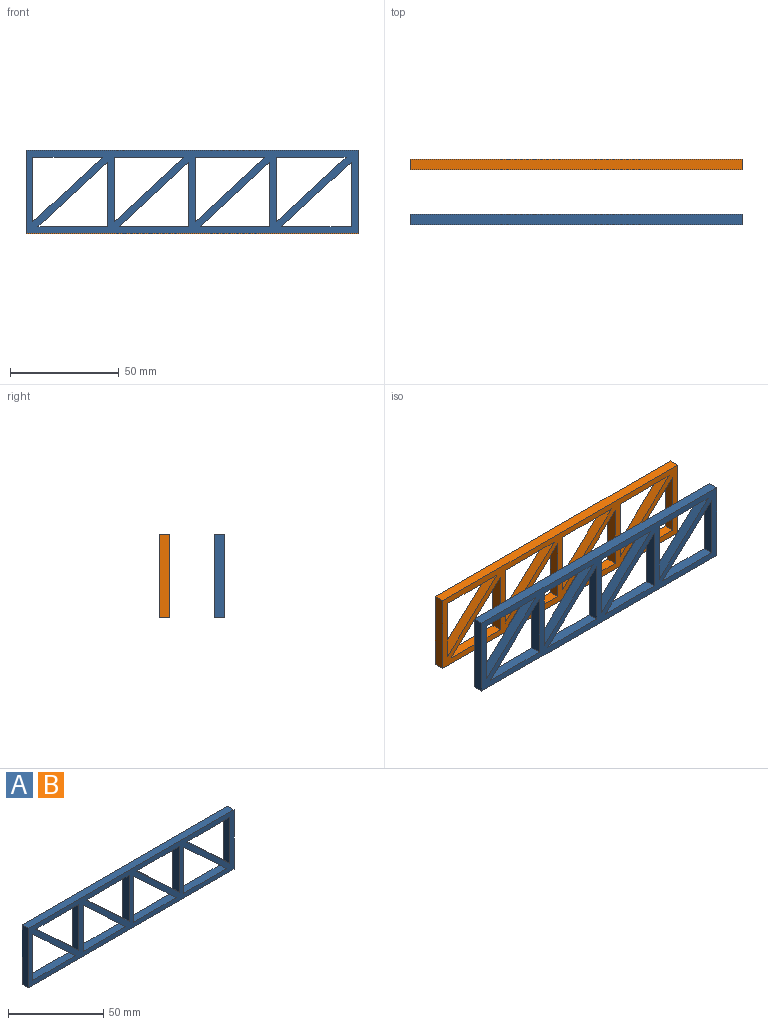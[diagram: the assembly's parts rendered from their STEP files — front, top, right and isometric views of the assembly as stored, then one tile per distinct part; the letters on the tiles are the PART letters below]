
ASSEMBLY  parts=2 mates=3
PART A: 30 faces, bbox 152.4x4.8x38.1 mm
  f0: plane 29.58x4.76mm, normal (1,0,0), area 140.9mm2, adj f1,f27,f28,f29
  f1: plane 31.8x29.58mm, normal (-0.68,0,-0.73), area 206.8mm2, adj f0,f27,f28,f29
  f2: plane 29.58x4.76mm, normal (1,0,0), area 140.9mm2, adj f3,f19,f28,f29
  f3: plane 31.8x29.58mm, normal (-0.68,0,-0.73), area 206.8mm2, adj f2,f19,f28,f29
  f4: plane 29.58x4.76mm, normal (1,0,0), area 140.9mm2, adj f5,f20,f28,f29
  f5: plane 31.8x29.58mm, normal (-0.68,0,-0.73), area 206.8mm2, adj f4,f20,f28,f29
  f6: plane 29.58x4.76mm, normal (1,0,0), area 140.9mm2, adj f7,f21,f28,f29
  f7: plane 31.8x29.58mm, normal (-0.68,0,-0.73), area 206.8mm2, adj f6,f21,f28,f29
  f8: plane 38.1x4.76mm, normal (-1,0,0), area 181.5mm2, adj f9,f22,f28,f29
  f9: plane 152.4x4.76mm, normal (0,0,-1), area 725.8mm2, adj f8,f10,f28,f29
  f10: plane 38.1x4.76mm, normal (1,0,0), area 181.5mm2, adj f9,f22,f28,f29
  f11: plane 31.8x29.58mm, normal (0.68,0,0.73), area 206.8mm2, adj f12,f23,f28,f29
  f12: plane 31.8x4.76mm, normal (0,0,-1), area 151.4mm2, adj f11,f23,f28,f29
  f13: plane 31.8x29.58mm, normal (0.68,0,0.73), area 206.8mm2, adj f14,f24,f28,f29
  f14: plane 31.8x4.76mm, normal (0,0,-1), area 151.4mm2, adj f13,f24,f28,f29
  f15: plane 31.8x29.58mm, normal (0.68,0,0.73), area 206.8mm2, adj f16,f25,f28,f29
  f16: plane 31.8x4.76mm, normal (0,0,-1), area 151.4mm2, adj f15,f25,f28,f29
  f17: plane 31.8x29.58mm, normal (0.68,0,0.73), area 206.8mm2, adj f18,f26,f28,f29
  f18: plane 31.8x4.76mm, normal (0,0,-1), area 151.4mm2, adj f17,f26,f28,f29
  f19: plane 31.8x4.76mm, normal (0,0,1), area 151.4mm2, adj f2,f3,f28,f29
  f20: plane 31.8x4.76mm, normal (0,0,1), area 151.4mm2, adj f4,f5,f28,f29
  f21: plane 31.8x4.76mm, normal (0,0,1), area 151.4mm2, adj f6,f7,f28,f29
  f22: plane 152.4x4.76mm, normal (0,0,1), area 725.8mm2, adj f8,f10,f28,f29
  f23: plane 29.58x4.76mm, normal (-1,0,0), area 140.9mm2, adj f11,f12,f28,f29
  f24: plane 29.58x4.76mm, normal (-1,0,0), area 140.9mm2, adj f13,f14,f28,f29
  f25: plane 29.58x4.76mm, normal (-1,0,0), area 140.9mm2, adj f15,f16,f28,f29
  f26: plane 29.58x4.76mm, normal (-1,0,0), area 140.9mm2, adj f17,f18,f28,f29
  f27: plane 31.8x4.76mm, normal (0,0,1), area 151.4mm2, adj f0,f1,f28,f29
  f28: plane 152.4x38.1mm, normal (0,-1,0), area 2043.6mm2, adj f0,f1,f2,f3,f4,f5,f6,f7
  f29: plane 152.4x38.1mm, normal (0,1,0), area 2043.6mm2, adj f0,f1,f2,f3,f4,f5,f6,f7
PART B: same geometry as A
PLACE A rot(axis=(0,0,1),180deg) t=(0,-3.5,20.45)mm fixed
PLACE B rot(axis=(0,0,1),180deg) t=(0,21.82,20.45)mm
MATE planar B.f8 <-> A.f8  axis (1,0,0) through (76.2,26.59,39.5)mm
MATE parallel B.f8 <-> A.f8  axis (1,0,0) through (76.2,24.21,20.45)mm
MATE planar B.f22 <-> A.f22  axis (0,0,1) through (0,24.21,39.5)mm
